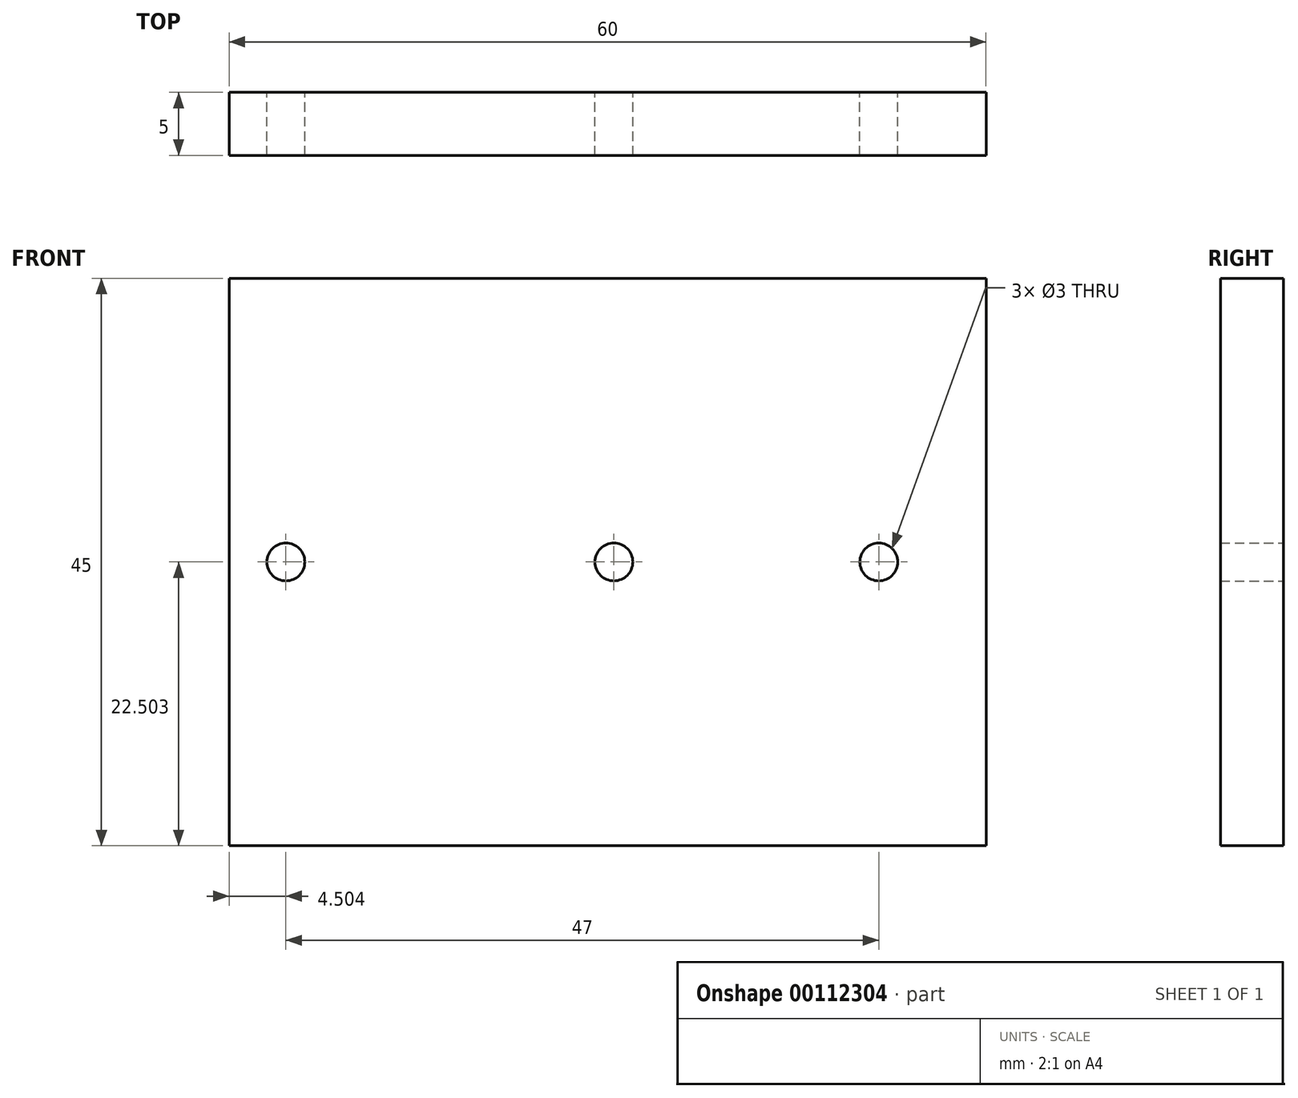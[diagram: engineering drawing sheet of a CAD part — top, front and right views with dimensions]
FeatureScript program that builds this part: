
annotation { "Feature Type Name" : "Feature", "Feature Type Description" : "" }
export const myFeature = defineFeature(function(context is Context, id is Id, definition is map)
    precondition{}
    {
        {
            var Q0;
            Q0=qCreatedBy(makeId("Front.planeOp"),FACE);
            var sketch = newSketch(context, id + "F0", { "sketchPlane" : qUnion([Q0])});
            skLineSegment(sketch, "E0.bottom", {"start": v(-43.19, 50) * mm, "end": v(16.81, 50) * mm});
            skLineSegment(sketch, "E0.top", {"start": v(-43.19, 5) * mm, "end": v(16.81, 5) * mm});
            skLineSegment(sketch, "E0.left", {"start": v(-43.19, 50) * mm, "end": v(-43.19, 5) * mm});
            skLineSegment(sketch, "E0.right", {"start": v(16.81, 50) * mm, "end": v(16.81, 5) * mm});
            skCircle(sketch, "E1", {"center": v(-38.69, 27.5) * mm, "radius": 1.5 * mm});
            skCircle(sketch, "E2", {"center": v(-12.69, 27.5) * mm, "radius": 1.5 * mm});
            skCircle(sketch, "E3", {"center": v(8.31, 27.5) * mm, "radius": 1.5 * mm});
            skSolve(sketch);
        }
        {
            var Q0;
            Q0=makeQuery(id+"F0.imprint","IMPRINT",FACE,{"disambiguationData":[TD([[makeQuery(id+"F0.imprint","IMPRINT",EDGE,{"derivedFrom":sQuery(id+"F0.wireOp",EDGE,"E0.bottom")}),-1.0]])]});
            extrude(context, id + "F1", {"entities" : qUnion([Q0]), "depth" : 5 * mm});
        }
    });
